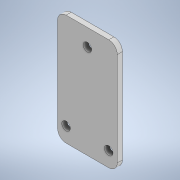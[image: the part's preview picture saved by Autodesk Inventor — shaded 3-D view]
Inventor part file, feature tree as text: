
AUTODESK INVENTOR PART (.ipt)
format: ipt  version: 2021 (Build 250183000, 183)  size: 109,056 bytes
history: native  units: mm
features: other x1, extrude x1, sketch x1
ambient origin geometry x8: Origin, YZ Plane, XZ Plane, XY Plane, X Axis, Y Axis, Z Axis, Center Point
bodies: Body1 (feature_tree)
feature tree (3):
  other  "Sólido1"
  extrude  "Extrusión1"  [1 undecoded]
  sketch  "Boceto1"  dims[d10=3.0mm d11=0.0mm]
note: 1 required parameter value undecoded (feature->parameter linkage not recoverable at this tier; creation-order binding heuristic only, values carry confidence <= 0.55)
